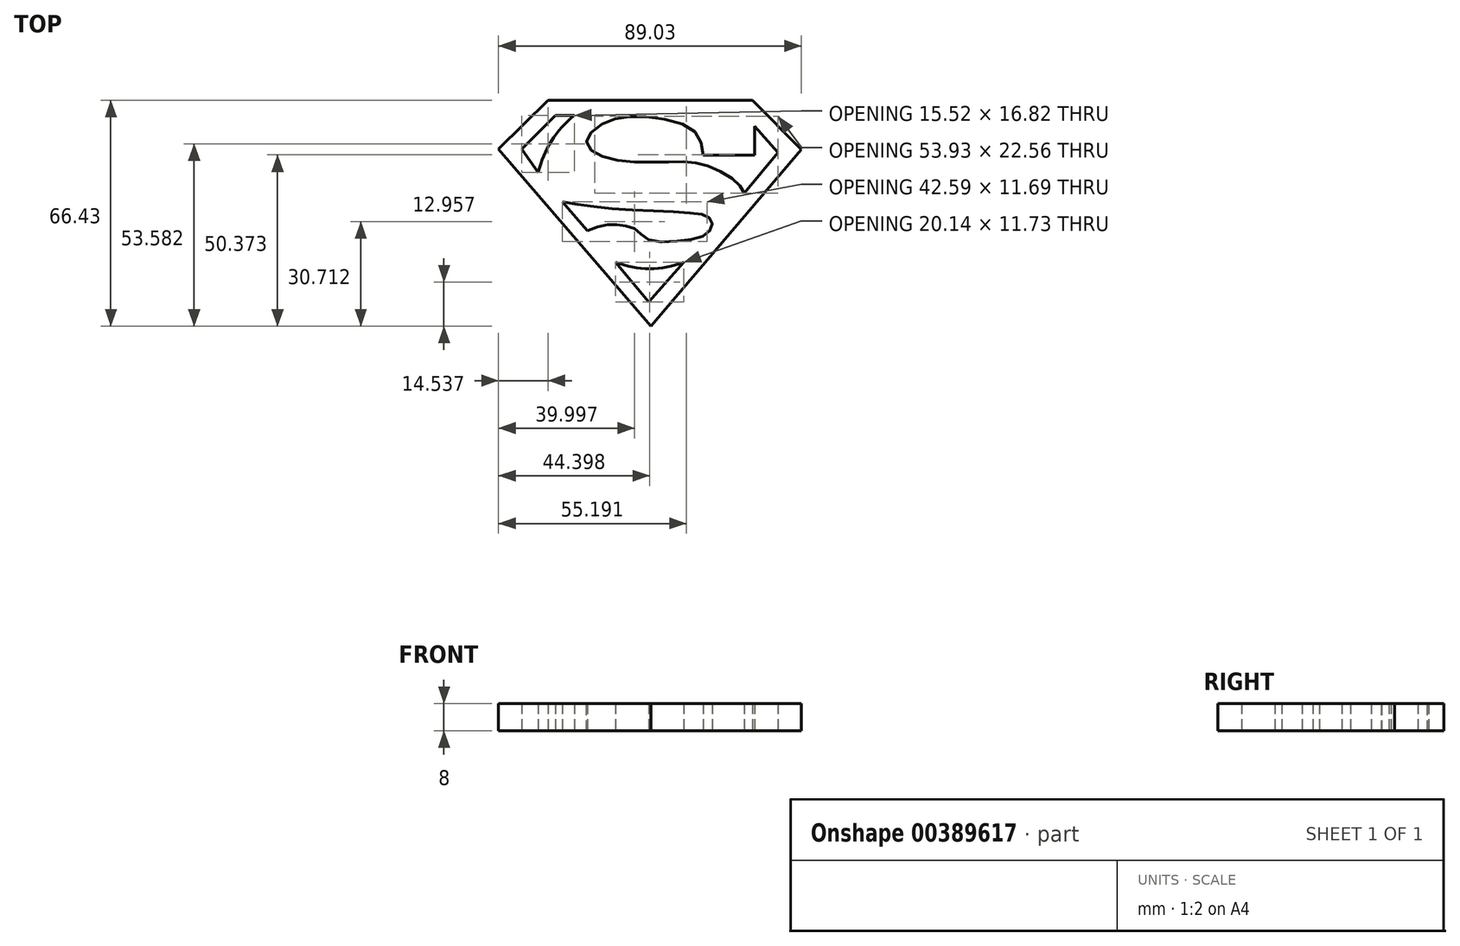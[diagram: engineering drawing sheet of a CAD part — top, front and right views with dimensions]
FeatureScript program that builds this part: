
annotation { "Feature Type Name" : "Feature", "Feature Type Description" : "" }
export const myFeature = defineFeature(function(context is Context, id is Id, definition is map)
    precondition{}
    {
        {
            var Q0;
            Q0=qCreatedBy(makeId("Top.planeOp"),FACE);
            var sketch = newSketch(context, id + "F0", { "sketchPlane" : qUnion([Q0])});
            skLineSegment(sketch, "E0", {"start": v(-25.56, 27.46) * mm, "end": v(-35.44, 17.57) * mm});
            skLineSegment(sketch, "E1", {"start": v(-35.44, 17.57) * mm, "end": v(-30.55, 10.64) * mm});
            skArc(sketch, "E2", {"start": v(-19.92, 27.46) * mm, "mid": v(-26.66, 19.95) * mm, "end": v(-30.55, 10.64) * mm});
            skLineSegment(sketch, "E3", {"start": v(-25.56, 27.46) * mm, "end": v(-19.92, 27.46) * mm});
            skLineSegment(sketch, "E4", {"start": v(16.58, 28.02) * mm, "end": v(22.68, 28.02) * mm});
            skArc(sketch, "E5", {"start": v(21.04, 23.93) * mm, "mid": v(22.48, 25.72) * mm, "end": v(22.68, 28.02) * mm});
            skArc(sketch, "E6", {"start": v(20.37, 23.93) * mm, "mid": v(18.8, 26.27) * mm, "end": v(16.58, 28.02) * mm});
            skFitSpline(sketch, "E7", {"points": [v(17.99, 15.8) * mm, v(15.23, 22.94) * mm, v(0.65, 27.03) * mm, v(-10.58, 25.47) * mm, v(-16.31, 20.11) * mm, v(-13.34, 16.1) * mm, v(-0.91, 13.71) * mm, v(12.26, 13.79) * mm, v(20, 12.3) * mm, v(27.66, 7.83) * mm, v(29.97, 4.56) * mm], "startDerivative": vector(-10.58, 85.82) * mm, "endDerivative": vector(25.28, -48.57) * mm});
            skLineSegment(sketch, "E8", {"start": v(29.97, 4.56) * mm, "end": v(39.94, 16.47) * mm});
            skLineSegment(sketch, "E9", {"start": v(39.94, 16.47) * mm, "end": v(33.1, 24.28) * mm});
            skLineSegment(sketch, "E10", {"start": v(33.1, 24.28) * mm, "end": v(33.1, 16.69) * mm});
            skLineSegment(sketch, "E11", {"start": v(17.99, 15.8) * mm, "end": v(33.1, 15.8) * mm});
            skLineSegment(sketch, "E12", {"start": v(33.1, 15.8) * mm, "end": v(33.1, 16.69) * mm});
            skLineSegment(sketch, "E13", {"start": v(-23.52, 2.03) * mm, "end": v(-16.13, -6.48) * mm});
            skFitSpline(sketch, "E14", {"points": [v(-23.52, 2.03) * mm, v(-8.25, 0) * mm, v(12.95, -1.13) * mm, v(19.35, -2.4) * mm, v(20.54, -4.33) * mm, v(19.28, -7.23) * mm, v(12.8, -9.24) * mm, v(1.64, -9.02) * mm, v(-1.7, -6.26) * mm, v(-5.87, -4.85) * mm, v(-10.26, -4.7) * mm, v(-16.13, -6.48) * mm], "startDerivative": vector(103.75, -17.08) * mm, "endDerivative": vector(-71.4, -26.6) * mm});
            skLineSegment(sketch, "E15", {"start": v(-7.9, -15.7) * mm, "end": v(1.9, -27.44) * mm});
            skLineSegment(sketch, "E16", {"start": v(1.9, -27.44) * mm, "end": v(12.25, -15.7) * mm});
            skArc(sketch, "E17", {"start": v(-7.9, -15.7) * mm, "mid": v(2.18, -17.66) * mm, "end": v(12.25, -15.7) * mm});
            skLineSegment(sketch, "E18", {"start": v(-27.62, 31.9) * mm, "end": v(32.35, 31.9) * mm});
            skLineSegment(sketch, "E19", {"start": v(32.35, 31.9) * mm, "end": v(46.8, 17.44) * mm});
            skLineSegment(sketch, "E20", {"start": v(46.8, 17.44) * mm, "end": v(2.6, -34.53) * mm});
            skLineSegment(sketch, "E21", {"start": v(2.6, -34.53) * mm, "end": v(-42.22, 17.49) * mm});
            skLineSegment(sketch, "E22", {"start": v(-42.22, 17.49) * mm, "end": v(-27.62, 31.9) * mm});
            skSolve(sketch);
        }
        {
            var Q0;
            Q0 = qSketchRegion(id + "F0", true);
            extrude(context, id + "F1", {"entities" : qUnion([Q0]), "depth" : 8 * mm});
        }
    });
